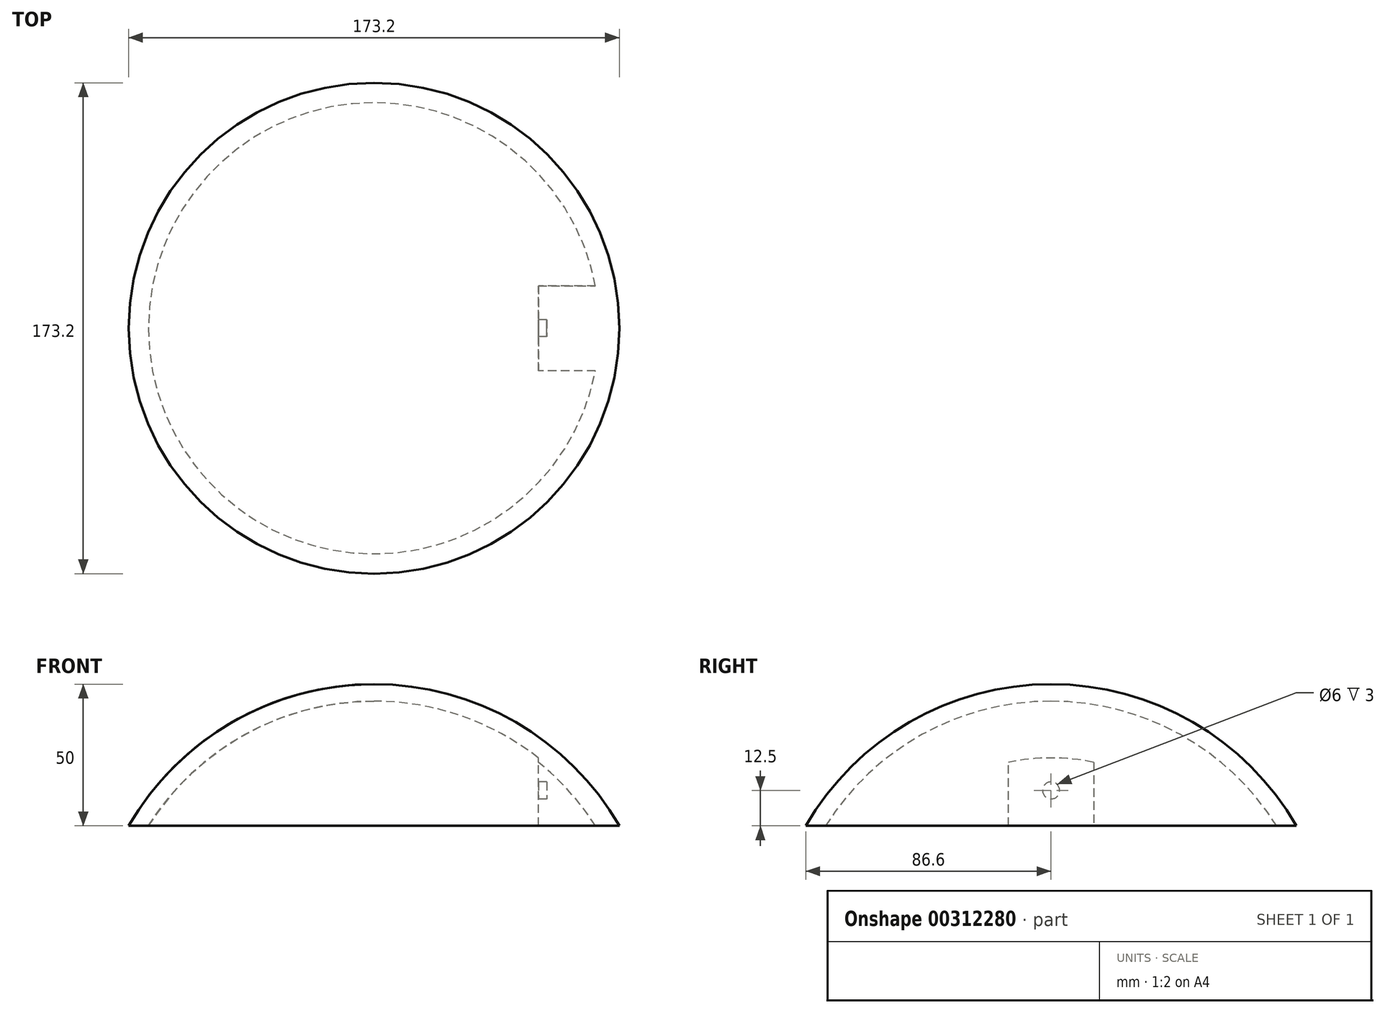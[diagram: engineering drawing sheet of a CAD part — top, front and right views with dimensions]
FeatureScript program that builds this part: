
annotation { "Feature Type Name" : "Feature", "Feature Type Description" : "" }
export const myFeature = defineFeature(function(context is Context, id is Id, definition is map)
    precondition{}
    {
        {
            var Q0;
            Q0=qCreatedBy(makeId("Front.planeOp"),FACE);
            var sketch = newSketch(context, id + "F0", { "sketchPlane" : qUnion([Q0])});
            skArc(sketch, "E0", {"start": v(0, 100) * mm, "mid": v(-50, 86.6) * mm, "end": v(-86.6, 50) * mm});
            skLineSegment(sketch, "E1", {"start": v(0, 100) * mm, "end": v(0, 50) * mm});
            skLineSegment(sketch, "E2", {"start": v(0, 50) * mm, "end": v(-86.6, 50) * mm});
            skSolve(sketch);
        }
        {
            var Q0;
            Q0=qSketchRegion(id+"F0",true);
            var Q1;
            Q1=sQuery(id+"F0.wireOp",EDGE,"E1");
            revolve(context, id + "F1", {"entities" : qUnion([Q0]), "axis" : qUnion([Q1]), "revolveType" : RevolveType.FULL});
        }
        {
            var Q0;
            Q0=makeQuery(id+"F1.opRevolve","SWEPT_FACE",FACE,{"disambiguationData":[OSD([sQuery(id+"F0.wireOp",EDGE,"E2")])]});
            shell(context, id + "F2", {"entities" : qUnion([Q0]), "thickness" : 6 * mm});
        }
        {
            var Q0;
            Q0=qCreatedBy(makeId("Right.planeOp"),FACE);
            cPlane(context, id + "F3", {"entities" : qUnion([Q0]), "cplaneType" : CPlaneType.OFFSET, "offset" : 58 * mm, "width" : 150 * mm, "height" : 150 * mm});
        }
        {
            var Q0;
            Q0=qCreatedBy(id+"F3.planeOp",FACE);
            var sketch = newSketch(context, id + "F4", { "sketchPlane" : qUnion([Q0])});
            skLineSegment(sketch, "E3.0", {"start": v(-15, 50) * mm, "end": v(15, 50) * mm});
            skLineSegment(sketch, "E4", {"start": v(-15, 50) * mm, "end": v(-15, 90) * mm});
            skLineSegment(sketch, "E5", {"start": v(-15, 90) * mm, "end": v(15, 90) * mm});
            skLineSegment(sketch, "E6", {"start": v(15, 90) * mm, "end": v(15, 50) * mm});
            skPoint(sketch, "E7.orphan", {"position": v(86.6, 50) * mm});
            skPoint(sketch, "E8.orphan", {"position": v(-86.6, 50) * mm});
            skSolve(sketch);
        }
        {
            var Q0;
            Q0=qSketchRegion(id+"F4",true);
            var Q1;
            Q1=makeQuery(id+"F2.opShell","OFFSET_FACE",FACE,{"disambiguationData":[OSD([sQuery(id+"F0.wireOp",EDGE,"E0")])]});
            extrude(context, id + "F5", {"entities" : qUnion([Q0]), "operationType" : NewBodyOperationType.ADD, "endBound" : BoundingType.UP_TO_SURFACE, "endBoundEntityFace" : qUnion([Q1]), "depth" : 25 * mm});
        }
        {
            var Q0;
            Q0=makeQuery(id+"F5.opExtrude","CAP_FACE",FACE,{"disambiguationData":[OSD([sQuery(id+"F4.wireOp",EDGE,"E3.0"),sQuery(id+"F4.wireOp",EDGE,"E4"),sQuery(id+"F4.wireOp",EDGE,"E5"),sQuery(id+"F4.wireOp",EDGE,"E6")])],"isStart":true});
            var sketch = newSketch(context, id + "F6", { "sketchPlane" : qUnion([Q0])});
            skCircle(sketch, "E9", {"center": v(0, 62.5) * mm, "radius": 3 * mm});
            skPoint(sketch, "E9.centerSnap0", {"position": v(0, 50) * mm});
            skSolve(sketch);
        }
        {
            var Q0;
            Q0=qSketchRegion(id+"F6",true);
            extrude(context, id + "F7", {"entities" : qUnion([Q0]), "operationType" : NewBodyOperationType.ADD, "oppositeDirection" : true, "depth" : 2 * mm});
        }
        {
            var Q0;
            Q0=qSketchRegion(id+"F6",true);
            extrude(context, id + "F8", {"entities" : qUnion([Q0]), "operationType" : NewBodyOperationType.REMOVE, "oppositeDirection" : true, "depth" : 3 * mm});
        }
    });
